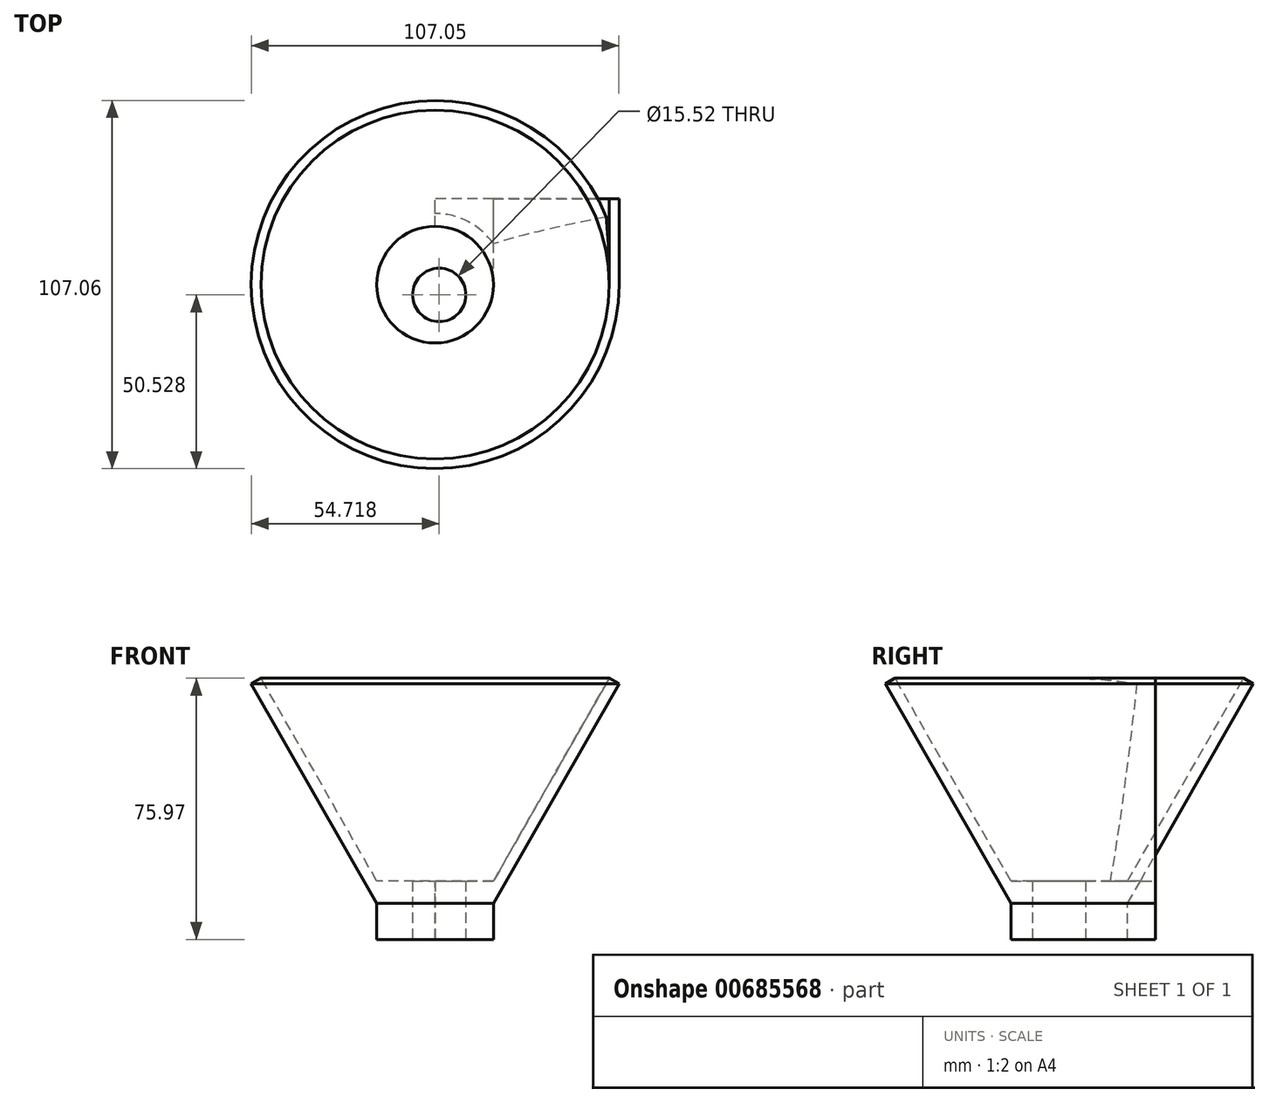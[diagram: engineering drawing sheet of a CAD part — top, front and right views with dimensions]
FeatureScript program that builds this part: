
annotation { "Feature Type Name" : "Feature", "Feature Type Description" : "" }
export const myFeature = defineFeature(function(context is Context, id is Id, definition is map)
    precondition{}
    {
        {
            var Q0;
            Q0=qCreatedBy(makeId("Front.planeOp"),FACE);
            var sketch = newSketch(context, id + "F0", { "sketchPlane" : qUnion([Q0])});
            skLineSegment(sketch, "E0", {"start": v(23.09, 53.08) * mm, "end": v(-10.65, -5.92) * mm});
            skLineSegment(sketch, "E1", {"start": v(-10.65, -5.92) * mm, "end": v(-27.62, -5.92) * mm});
            skLineSegment(sketch, "E2", {"start": v(-27.62, -5.92) * mm, "end": v(-27.62, -22.89) * mm});
            skLineSegment(sketch, "E3", {"start": v(-27.62, -22.89) * mm, "end": v(-10.65, -22.89) * mm});
            skLineSegment(sketch, "E4", {"start": v(-10.65, -22.89) * mm, "end": v(-10.65, -12.43) * mm});
            skLineSegment(sketch, "E5", {"start": v(-10.65, -12.43) * mm, "end": v(25.9, 51.5) * mm});
            skLineSegment(sketch, "E6", {"start": v(25.9, 51.5) * mm, "end": v(23.09, 53.08) * mm});
            skSolve(sketch);
        }
        {
            var Q0;
            Q0=makeQuery(id+"F0.imprint","IMPRINT",FACE,{"disambiguationData":[TD([[makeQuery(id+"F0.imprint","IMPRINT",EDGE,{"derivedFrom":sQuery(id+"F0.wireOp",EDGE,"E0")}),1.0]])]});
            extrude(context, id + "F1", {"entities" : qUnion([Q0]), "depth" : 25 * mm, "offsetDistance" : 25 * mm});
        }
        {
            var Q0;
            Q0=makeQuery(id+"F1.opExtrude","CAP_FACE",FACE,{"disambiguationData":[OSD([sQuery(id+"F0.wireOp",EDGE,"E0"),sQuery(id+"F0.wireOp",EDGE,"E1"),sQuery(id+"F0.wireOp",EDGE,"E2"),sQuery(id+"F0.wireOp",EDGE,"E3"),sQuery(id+"F0.wireOp",EDGE,"E4"),sQuery(id+"F0.wireOp",EDGE,"E5"),sQuery(id+"F0.wireOp",EDGE,"E6")])],"isStart":false});
            var Q1;
            Q1=makeQuery(id+"F1.opExtrude","CAP_EDGE",EDGE,{"disambiguationData":[OSD([sQuery(id+"F0.wireOp",EDGE,"E2")])],"isStart":false});
            revolve(context, id + "F2", {"operationType" : NewBodyOperationType.ADD, "surfaceOperationType" : NewSurfaceOperationType.NEW, "entities" : qUnion([Q0]), "axis" : qUnion([Q1]), "revolveType" : RevolveType.FULL});
        }
        {
            var Q0;
            {var subQ0=sQuery(id+"F0.wireOp",EDGE,"E3");Q0=makeQuery(id+"F2.boolean.opBoolean","MERGE",FACE,{"derivedFrom":[makeQuery(id+"F1.opExtrude","SWEPT_FACE",FACE,{"disambiguationData":[OSD([subQ0])]}),makeQuery(id+"F2.opRevolve","SWEPT_FACE",FACE,{"disambiguationData":[OSD([subQ0])]})]});}
            var sketch = newSketch(context, id + "F3", { "sketchPlane" : qUnion([Q0])});
            skCircle(sketch, "E7", {"center": v(-26.43, 28) * mm, "radius": 7.76 * mm});
            skSolve(sketch);
        }
        {
            var Q0;
            Q0 = qSketchRegion(id + "F3", true);
            extrude(context, id + "F4", {"entities" : qUnion([Q0]), "operationType" : NewBodyOperationType.REMOVE, "oppositeDirection" : true, "depth" : 25 * mm, "offsetDistance" : 25 * mm});
        }
    });
